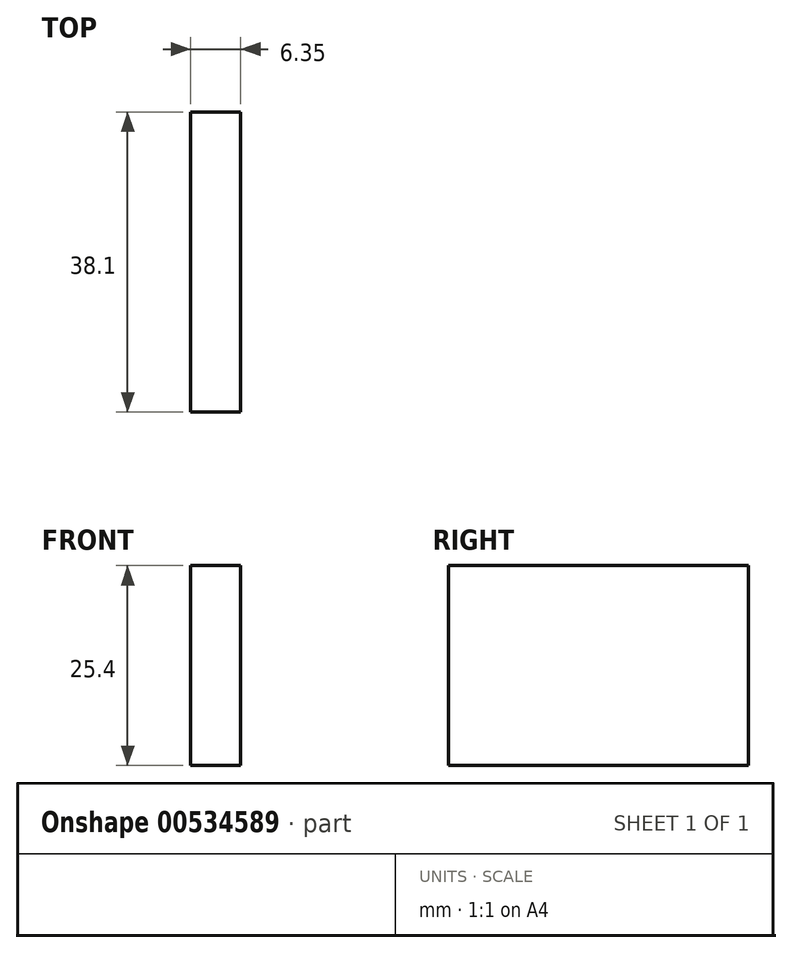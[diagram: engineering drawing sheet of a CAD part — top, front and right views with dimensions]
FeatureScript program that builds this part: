
annotation { "Feature Type Name" : "Feature", "Feature Type Description" : "" }
export const myFeature = defineFeature(function(context is Context, id is Id, definition is map)
    precondition{}
    {
        {
            var Q0;
            Q0=qCreatedBy(makeId("Top.planeOp"),FACE);
            var sketch = newSketch(context, id + "F0", { "sketchPlane" : qUnion([Q0])});
            skLineSegment(sketch, "E0.bottom", {"start": v(0, 0) * mm, "end": v(-6.35, 0) * mm});
            skLineSegment(sketch, "E0.top", {"start": v(0, 38.1) * mm, "end": v(-6.35, 38.1) * mm});
            skLineSegment(sketch, "E0.left", {"start": v(0, 0) * mm, "end": v(0, 38.1) * mm});
            skLineSegment(sketch, "E0.right", {"start": v(-6.35, 0) * mm, "end": v(-6.35, 38.1) * mm});
            skSolve(sketch);
        }
        {
            var Q0;
            Q0=makeQuery(id+"F0.imprint","IMPRINT",FACE,{"disambiguationData":[TD([[makeQuery(id+"F0.imprint","IMPRINT",EDGE,{"derivedFrom":sQuery(id+"F0.wireOp",EDGE,"E0.bottom")}),-1.0]])]});
            extrude(context, id + "F1", {"entities" : qUnion([Q0]), "depth" : 25.4 * mm, "offsetDistance" : 25.4 * mm});
        }
    });
